# Revit family: FP_Revit_18_CE604DTB1_Cooktop_90000826A
name_source: partatom
category: Specialty Equipment
revit_build: Autodesk Revit 2018 (Build: 20170223_1515(x64)
units: mm (PartAtom-declared; Revit-internal decimal feet)

## family parameters
Always vertical = Yes
Cut with Voids When Loaded = Yes
OmniClass Number = 23.40.40.14.17.11
OmniClass Title = Cookers, Ovens, Stoves
Part Type = Normal
Room Calculation Point = No
Round Connector Dimension = Use Diameter
Shared = No
Work Plane-Based = No

## types (1)
- FP_Revit_18_CE604DTB1_Cooktop_90000826A
    Cavity - Depth = 490 mm  [stored 1.60761 ft]
    Cavity - Height = 58 mm  [stored 0.190289 ft]
    Cavity - Width = 560 mm  [stored 1.83727 ft]
    Chassis - Depth = 480 mm  [stored 1.5748 ft]
    Chassis - Height = 48 mm  [stored 0.15748 ft]
    Chassis - Width = 552 mm  [stored 1.81102 ft]
    Clearance - Below Combustible = 68 mm
    Clearance - Overhead Rangehood = 650 mm  [stored 2.13255 ft]
    Clearance - Rear Combustible = 55 mm  [stored 0.180446 ft]
    Clearance - Side Combustible = 85 mm  [stored 0.278871 ft]
    Connector Note - Electrical = 220-240/380-415 V, 2 Phase, 50 Hz, 28 A
    Description = 60cm Electric Cooktop
    Manufacturer = Fisher & Paykel Appliances
    Material - Body = Fisher & Paykel - Grey
    Material - Cooktop = Fisher & Paykel - Glass, Black
    Material - Graphics = Fisher & Paykel - Graphics Grey
    Model = CE604DTB1
    Product - Depth = 530 mm  [stored 1.73885 ft]
    Product - Height = 63 mm  [stored 0.206693 ft]
    Product - Width = 600 mm
    URL = www.fisherpaykel.com
    Visibility - Clearance Required = Yes

note: [stored X ft] marks values corroborated as IEEE doubles in the binary element streams (Revit-internal decimal feet)

## geometry (parser evidence)
native form markers: Sweep x8
no freeform markers — native parametric forms only
